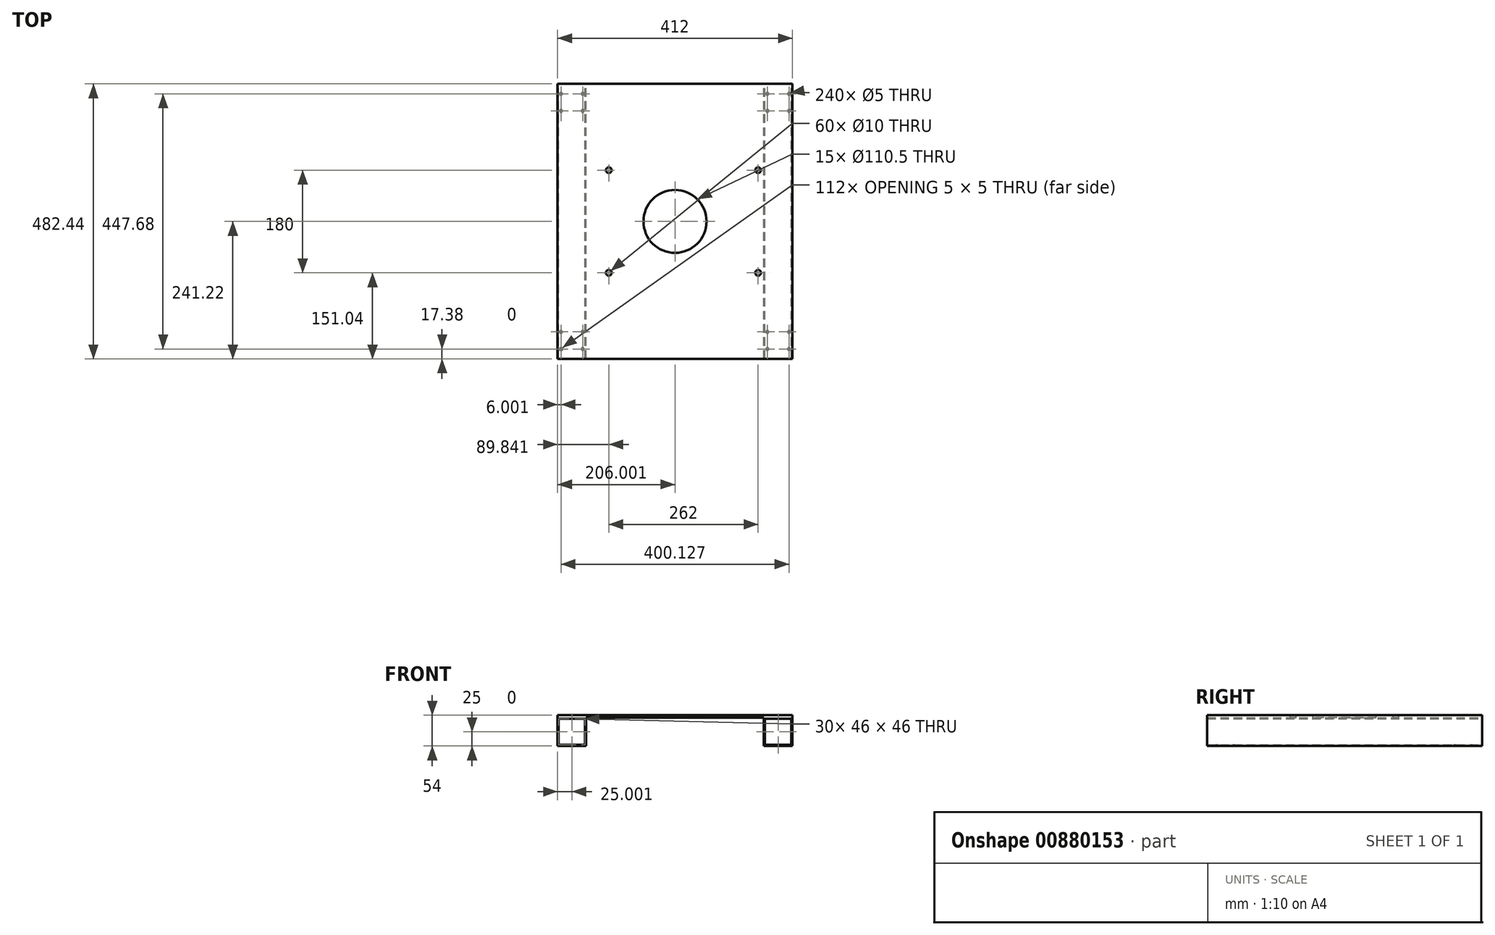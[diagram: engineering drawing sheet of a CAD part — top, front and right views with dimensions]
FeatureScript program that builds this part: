
annotation { "Feature Type Name" : "Feature", "Feature Type Description" : "" }
export const myFeature = defineFeature(function(context is Context, id is Id, definition is map)
    precondition{}
    {
        {
            var Q0;
            Q0=qCreatedBy(makeId("Front.planeOp"),FACE);
            var sketch = newSketch(context, id + "F0", { "sketchPlane" : qUnion([Q0])});
            skLineSegment(sketch, "E0", {"start": v(352.9, 0) * mm, "end": v(-59.1, 0) * mm});
            skLineSegment(sketch, "E1", {"start": v(-59.1, 0) * mm, "end": v(-59.1, -4) * mm});
            skLineSegment(sketch, "E2", {"start": v(-59.1, -4) * mm, "end": v(352.9, -4) * mm});
            skLineSegment(sketch, "E3", {"start": v(352.9, -4) * mm, "end": v(352.9, 0) * mm});
            skLineSegment(sketch, "E4", {"start": v(-59.1, -4) * mm, "end": v(-59.1, -54) * mm});
            skLineSegment(sketch, "E5", {"start": v(-59.1, -54) * mm, "end": v(-9.1, -54) * mm});
            skLineSegment(sketch, "E6", {"start": v(-9.1, -54) * mm, "end": v(-9.1, -4) * mm});
            skLineSegment(sketch, "E7", {"start": v(352.9, -4) * mm, "end": v(352.9, -54) * mm});
            skLineSegment(sketch, "E8", {"start": v(352.9, -54) * mm, "end": v(302.9, -54) * mm});
            skLineSegment(sketch, "E9", {"start": v(302.9, -54) * mm, "end": v(302.9, -4) * mm});
            skLineSegment(sketch, "E10", {"start": v(-59.1, -4) * mm, "end": v(-57.1, -4) * mm});
            skLineSegment(sketch, "E11", {"start": v(-57.1, -4) * mm, "end": v(-57.1, -52) * mm});
            skLineSegment(sketch, "E12", {"start": v(-57.1, -52) * mm, "end": v(-11.1, -52) * mm});
            skLineSegment(sketch, "E13", {"start": v(-11.1, -52) * mm, "end": v(-11.1, -6) * mm});
            skLineSegment(sketch, "E14", {"start": v(-11.1, -6) * mm, "end": v(-57.1, -6) * mm});
            skLineSegment(sketch, "E15", {"start": v(302.9, -4) * mm, "end": v(304.9, -4) * mm});
            skLineSegment(sketch, "E16", {"start": v(304.9, -4) * mm, "end": v(304.9, -52) * mm});
            skLineSegment(sketch, "E17", {"start": v(304.9, -52) * mm, "end": v(350.9, -52) * mm});
            skLineSegment(sketch, "E18", {"start": v(350.9, -52) * mm, "end": v(350.9, -6) * mm});
            skLineSegment(sketch, "E19", {"start": v(350.9, -6) * mm, "end": v(304.9, -6) * mm});
            skSolve(sketch);
        }
        {
            var Q0;
            {var subQ1=sQuery(id+"F0.wireOp",EDGE,"E7");Q0=makeQuery(id+"F0.imprint","IMPRINT",FACE,{"disambiguationData":[TD([[makeQuery(id+"F0.imprint","IMPRINT",EDGE,{"derivedFrom":subQ1}),-1.0]])]});}
            var Q1;
            Q1=makeQuery(id+"F0.imprint","IMPRINT",FACE,{"disambiguationData":[TD([[makeQuery(id+"F0.imprint","IMPRINT",EDGE,{"derivedFrom":sQuery(id+"F0.wireOp",EDGE,"E0")}),1.0]])]});
            var Q2;
            Q2=makeQuery(id+"F0.imprint","IMPRINT",FACE,{"disambiguationData":[TD([[makeQuery(id+"F0.imprint","IMPRINT",EDGE,{"derivedFrom":sQuery(id+"F0.wireOp",EDGE,"E4")}),1.0]])]});
            extrude(context, id + "F1", {"entities" : qUnion([Q0, Q1, Q2]), "depth" : 482.44 * mm, "offsetDistance" : 25 * mm});
        }
        {
            var Q0;
            Q0=makeQuery(id+"F1.opExtrude","SWEPT_FACE",FACE,{"disambiguationData":[OSD([sQuery(id+"F0.wireOp",EDGE,"E0")])]});
            var sketch = newSketch(context, id + "F2", { "sketchPlane" : qUnion([Q0])});
            skLineSegment(sketch, "E20", {"start": v(146.9, 0) * mm, "end": v(146.9, -482.44) * mm});
            skLineSegment(sketch, "E21", {"start": v(-59.1, -241.22) * mm, "end": v(352.9, -241.22) * mm});
            skCircle(sketch, "E22", {"center": v(146.9, -241.22) * mm, "radius": 55.25 * mm});
            skSolve(sketch);
        }
        {
            var Q0;
            Q0 = qSketchRegion(id + "F2", true);
            extrude(context, id + "F3", {"entities" : qUnion([Q0]), "operationType" : NewBodyOperationType.REMOVE, "oppositeDirection" : true, "depth" : 25 * mm, "offsetDistance" : 25 * mm});
        }
        {
            var Q0;
            Q0=makeQuery(id+"F1.opExtrude","SWEPT_FACE",FACE,{"disambiguationData":[OSD([sQuery(id+"F0.wireOp",EDGE,"E5")])]});
            var sketch = newSketch(context, id + "F4", { "sketchPlane" : qUnion([Q0])});
            skLineSegment(sketch, "E23", {"start": v(-59.1, 0) * mm, "end": v(-59.1, 17.38) * mm});
            skLineSegment(sketch, "E24", {"start": v(-59.1, 17.38) * mm, "end": v(-52.97, 17.38) * mm});
            skLineSegment(sketch, "E25", {"start": v(-52.97, 17.38) * mm, "end": v(-52.97, 47.38) * mm});
            skLineSegment(sketch, "E26", {"start": v(-52.97, 47.38) * mm, "end": v(-14.97, 47.38) * mm});
            skLineSegment(sketch, "E27", {"start": v(-14.97, 47.38) * mm, "end": v(-14.97, 17.38) * mm});
            skCircle(sketch, "E28", {"center": v(-52.97, 47.38) * mm, "radius": 2.5 * mm});
            skCircle(sketch, "E29", {"center": v(-52.97, 17.38) * mm, "radius": 2.5 * mm});
            skCircle(sketch, "E30", {"center": v(-14.97, 47.38) * mm, "radius": 2.5 * mm});
            skCircle(sketch, "E31", {"center": v(-14.97, 17.38) * mm, "radius": 2.5 * mm});
            skLineSegment(sketch, "E32", {"start": v(302.9, 0) * mm, "end": v(302.9, 17.38) * mm});
            skLineSegment(sketch, "E33", {"start": v(302.9, 17.38) * mm, "end": v(309.03, 17.38) * mm});
            skLineSegment(sketch, "E34", {"start": v(309.03, 17.38) * mm, "end": v(309.03, 47.38) * mm});
            skLineSegment(sketch, "E35", {"start": v(309.03, 47.38) * mm, "end": v(347.03, 47.38) * mm});
            skLineSegment(sketch, "E36", {"start": v(347.03, 47.38) * mm, "end": v(347.03, 17.38) * mm});
            skCircle(sketch, "E37", {"center": v(309.03, 47.38) * mm, "radius": 2.5 * mm});
            skCircle(sketch, "E38", {"center": v(309.03, 17.38) * mm, "radius": 2.5 * mm});
            skCircle(sketch, "E39", {"center": v(347.03, 47.38) * mm, "radius": 2.5 * mm});
            skCircle(sketch, "E40", {"center": v(347.03, 17.38) * mm, "radius": 2.5 * mm});
            skSolve(sketch);
        }
        {
            var Q0;
            {var subQ0=sQuery(id+"F4.wireOp",EDGE,"E27");var subQ1=sQuery(id+"F4.wireOp",EDGE,"E26");var subQ2=makeQuery(id+"F4.imprint","INTERSECT",VERTEX,{"derivedFrom":[subQ1,subQ0]});Q0=makeQuery(id+"F4.imprint","IMPRINT",FACE,{"disambiguationData":[TD([[makeQuery(id+"F4.imprint","IMPRINT",EDGE,{"disambiguationData":[TD([[subQ2,1.0]])],"derivedFrom":subQ1}),-1.0]])]});}
            var Q1;
            {var subQ0=sQuery(id+"F4.wireOp",EDGE,"E27");var subQ1=sQuery(id+"F4.wireOp",EDGE,"E26");var subQ2=makeQuery(id+"F4.imprint","INTERSECT",VERTEX,{"derivedFrom":[subQ1,subQ0]});Q1=makeQuery(id+"F4.imprint","IMPRINT",FACE,{"disambiguationData":[TD([[makeQuery(id+"F4.imprint","IMPRINT",EDGE,{"disambiguationData":[TD([[subQ2,1.0]])],"derivedFrom":subQ1}),1.0]])]});}
            var Q2;
            {var subQ0=sQuery(id+"F4.wireOp",EDGE,"E26");var subQ1=sQuery(id+"F4.wireOp",EDGE,"E25");var subQ2=makeQuery(id+"F4.imprint","INTERSECT",VERTEX,{"derivedFrom":[subQ1,subQ0]});Q2=makeQuery(id+"F4.imprint","IMPRINT",FACE,{"disambiguationData":[TD([[makeQuery(id+"F4.imprint","IMPRINT",EDGE,{"disambiguationData":[TD([[subQ2,1.0]])],"derivedFrom":subQ1}),1.0]])]});}
            var Q3;
            {var subQ0=sQuery(id+"F4.wireOp",EDGE,"E26");var subQ1=sQuery(id+"F4.wireOp",EDGE,"E25");var subQ2=makeQuery(id+"F4.imprint","INTERSECT",VERTEX,{"derivedFrom":[subQ1,subQ0]});Q3=makeQuery(id+"F4.imprint","IMPRINT",FACE,{"disambiguationData":[TD([[makeQuery(id+"F4.imprint","IMPRINT",EDGE,{"disambiguationData":[TD([[subQ2,1.0]])],"derivedFrom":subQ1}),-1.0]])]});}
            var Q4;
            {var subQ0=sQuery(id+"F4.wireOp",EDGE,"E25");var subQ1=sQuery(id+"F4.wireOp",EDGE,"E24");var subQ2=makeQuery(id+"F4.imprint","INTERSECT",VERTEX,{"derivedFrom":[subQ1,subQ0]});Q4=makeQuery(id+"F4.imprint","IMPRINT",FACE,{"disambiguationData":[TD([[makeQuery(id+"F4.imprint","IMPRINT",EDGE,{"disambiguationData":[TD([[subQ2,1.0]])],"derivedFrom":subQ1}),1.0]])]});}
            var Q5;
            {var subQ0=sQuery(id+"F4.wireOp",EDGE,"E25");var subQ1=sQuery(id+"F4.wireOp",EDGE,"E24");var subQ2=makeQuery(id+"F4.imprint","INTERSECT",VERTEX,{"derivedFrom":[subQ1,subQ0]});Q5=makeQuery(id+"F4.imprint","IMPRINT",FACE,{"disambiguationData":[TD([[makeQuery(id+"F4.imprint","IMPRINT",EDGE,{"disambiguationData":[TD([[subQ2,1.0]])],"derivedFrom":subQ1}),-1.0]])]});}
            var Q6;
            Q6=makeQuery(id+"F4.imprint","IMPRINT",FACE,{"disambiguationData":[TD([[makeQuery(id+"F4.imprint","IMPRINT",EDGE,{"derivedFrom":sQuery(id+"F4.wireOp",EDGE,"E31")}),1.0]])]});
            var Q7;
            Q7=sQuery(id+"F4.wireOp",EDGE,"E28");
            var Q8;
            Q8=sQuery(id+"F4.wireOp",EDGE,"E30");
            var Q9;
            Q9=sQuery(id+"F4.wireOp",EDGE,"E29");
            var Q10;
            Q10=sQuery(id+"F4.wireOp",EDGE,"E31");
            extrude(context, id + "F5", {"entities" : qUnion([Q0, Q1, Q2, Q3, Q4, Q5, Q6]), "operationType" : NewBodyOperationType.REMOVE, "surfaceEntities" : qUnion([Q7, Q8, Q9, Q10]), "oppositeDirection" : true, "depth" : 25 * mm, "offsetDistance" : 25 * mm});
        }
        {
            var Q0;
            Q0=makeQuery(id+"F1.opExtrude","SWEPT_FACE",FACE,{"disambiguationData":[OSD([sQuery(id+"F0.wireOp",EDGE,"E5")])]});
            var sketch = newSketch(context, id + "F6", { "sketchPlane" : qUnion([Q0])});
            skLineSegment(sketch, "E41", {"start": v(302.87, 482.44) * mm, "end": v(302.87, 465.06) * mm});
            skLineSegment(sketch, "E42", {"start": v(302.87, 465.06) * mm, "end": v(309, 465.06) * mm});
            skLineSegment(sketch, "E43", {"start": v(309, 465.06) * mm, "end": v(309, 435.06) * mm});
            skLineSegment(sketch, "E44", {"start": v(309, 435.06) * mm, "end": v(347, 435.06) * mm});
            skLineSegment(sketch, "E45", {"start": v(347, 435.06) * mm, "end": v(347, 465.06) * mm});
            skCircle(sketch, "E46", {"center": v(309, 465.06) * mm, "radius": 2.5 * mm});
            skCircle(sketch, "E47", {"center": v(309, 435.06) * mm, "radius": 2.5 * mm});
            skCircle(sketch, "E48", {"center": v(347, 465.06) * mm, "radius": 2.5 * mm});
            skCircle(sketch, "E49", {"center": v(347, 435.06) * mm, "radius": 2.5 * mm});
            skLineSegment(sketch, "E50", {"start": v(-59.23, 482.44) * mm, "end": v(-59.23, 465.06) * mm});
            skLineSegment(sketch, "E51", {"start": v(-59.23, 465.06) * mm, "end": v(-53.1, 465.06) * mm});
            skLineSegment(sketch, "E52", {"start": v(-53.1, 465.06) * mm, "end": v(-53.1, 435.06) * mm});
            skLineSegment(sketch, "E53", {"start": v(-53.1, 435.06) * mm, "end": v(-15.1, 435.06) * mm});
            skLineSegment(sketch, "E54", {"start": v(-15.1, 435.06) * mm, "end": v(-15.1, 465.06) * mm});
            skCircle(sketch, "E55", {"center": v(-53.1, 465.06) * mm, "radius": 2.5 * mm});
            skCircle(sketch, "E56", {"center": v(-53.1, 435.06) * mm, "radius": 2.5 * mm});
            skCircle(sketch, "E57", {"center": v(-15.1, 465.06) * mm, "radius": 2.5 * mm});
            skCircle(sketch, "E58", {"center": v(-15.1, 435.06) * mm, "radius": 2.5 * mm});
            skSolve(sketch);
        }
        {
            var Q0;
            Q0=makeQuery(id+"F6.imprint","IMPRINT",FACE,{"disambiguationData":[TD([[makeQuery(id+"F6.imprint","IMPRINT",EDGE,{"derivedFrom":sQuery(id+"F6.wireOp",EDGE,"E48")}),1.0]])]});
            var Q1;
            {var subQ0=sQuery(id+"F6.wireOp",EDGE,"E45");var subQ1=sQuery(id+"F6.wireOp",EDGE,"E44");var subQ2=makeQuery(id+"F6.imprint","INTERSECT",VERTEX,{"derivedFrom":[subQ1,subQ0]});Q1=makeQuery(id+"F6.imprint","IMPRINT",FACE,{"disambiguationData":[TD([[makeQuery(id+"F6.imprint","IMPRINT",EDGE,{"disambiguationData":[TD([[subQ2,1.0]])],"derivedFrom":subQ1}),-1.0]])]});}
            var Q2;
            {var subQ0=sQuery(id+"F6.wireOp",EDGE,"E45");var subQ1=sQuery(id+"F6.wireOp",EDGE,"E44");var subQ2=makeQuery(id+"F6.imprint","INTERSECT",VERTEX,{"derivedFrom":[subQ1,subQ0]});Q2=makeQuery(id+"F6.imprint","IMPRINT",FACE,{"disambiguationData":[TD([[makeQuery(id+"F6.imprint","IMPRINT",EDGE,{"disambiguationData":[TD([[subQ2,1.0]])],"derivedFrom":subQ1}),1.0]])]});}
            var Q3;
            {var subQ0=sQuery(id+"F6.wireOp",EDGE,"E44");var subQ1=sQuery(id+"F6.wireOp",EDGE,"E43");var subQ2=makeQuery(id+"F6.imprint","INTERSECT",VERTEX,{"derivedFrom":[subQ1,subQ0]});Q3=makeQuery(id+"F6.imprint","IMPRINT",FACE,{"disambiguationData":[TD([[makeQuery(id+"F6.imprint","IMPRINT",EDGE,{"disambiguationData":[TD([[subQ2,1.0]])],"derivedFrom":subQ1}),-1.0]])]});}
            var Q4;
            {var subQ0=sQuery(id+"F6.wireOp",EDGE,"E44");var subQ1=sQuery(id+"F6.wireOp",EDGE,"E43");var subQ2=makeQuery(id+"F6.imprint","INTERSECT",VERTEX,{"derivedFrom":[subQ1,subQ0]});Q4=makeQuery(id+"F6.imprint","IMPRINT",FACE,{"disambiguationData":[TD([[makeQuery(id+"F6.imprint","IMPRINT",EDGE,{"disambiguationData":[TD([[subQ2,1.0]])],"derivedFrom":subQ1}),1.0]])]});}
            var Q5;
            {var subQ0=sQuery(id+"F6.wireOp",EDGE,"E43");var subQ1=sQuery(id+"F6.wireOp",EDGE,"E42");var subQ2=makeQuery(id+"F6.imprint","INTERSECT",VERTEX,{"derivedFrom":[subQ1,subQ0]});Q5=makeQuery(id+"F6.imprint","IMPRINT",FACE,{"disambiguationData":[TD([[makeQuery(id+"F6.imprint","IMPRINT",EDGE,{"disambiguationData":[TD([[subQ2,1.0]])],"derivedFrom":subQ1}),-1.0]])]});}
            var Q6;
            {var subQ0=sQuery(id+"F6.wireOp",EDGE,"E43");var subQ1=sQuery(id+"F6.wireOp",EDGE,"E42");var subQ2=makeQuery(id+"F6.imprint","INTERSECT",VERTEX,{"derivedFrom":[subQ1,subQ0]});Q6=makeQuery(id+"F6.imprint","IMPRINT",FACE,{"disambiguationData":[TD([[makeQuery(id+"F6.imprint","IMPRINT",EDGE,{"disambiguationData":[TD([[subQ2,1.0]])],"derivedFrom":subQ1}),1.0]])]});}
            var Q7;
            Q7=sQuery(id+"F6.wireOp",EDGE,"E46");
            var Q8;
            Q8=sQuery(id+"F6.wireOp",EDGE,"E47");
            var Q9;
            Q9=sQuery(id+"F6.wireOp",EDGE,"E49");
            var Q10;
            Q10=sQuery(id+"F6.wireOp",EDGE,"E48");
            extrude(context, id + "F7", {"entities" : qUnion([Q0, Q1, Q2, Q3, Q4, Q5, Q6]), "operationType" : NewBodyOperationType.REMOVE, "surfaceEntities" : qUnion([Q7, Q8, Q9, Q10]), "oppositeDirection" : true, "depth" : 25 * mm, "offsetDistance" : 25 * mm});
        }
        {
            var Q0;
            Q0=makeQuery(id+"F6.imprint","IMPRINT",FACE,{"disambiguationData":[TD([[makeQuery(id+"F6.imprint","IMPRINT",EDGE,{"derivedFrom":sQuery(id+"F6.wireOp",EDGE,"E57")}),1.0]])]});
            var Q1;
            {var subQ0=sQuery(id+"F6.wireOp",EDGE,"E52");var subQ1=sQuery(id+"F6.wireOp",EDGE,"E51");var subQ2=makeQuery(id+"F6.imprint","INTERSECT",VERTEX,{"derivedFrom":[subQ1,subQ0]});Q1=makeQuery(id+"F6.imprint","IMPRINT",FACE,{"disambiguationData":[TD([[makeQuery(id+"F6.imprint","IMPRINT",EDGE,{"disambiguationData":[TD([[subQ2,1.0]])],"derivedFrom":subQ1}),1.0]])]});}
            var Q2;
            {var subQ0=sQuery(id+"F6.wireOp",EDGE,"E52");var subQ1=sQuery(id+"F6.wireOp",EDGE,"E51");var subQ2=makeQuery(id+"F6.imprint","INTERSECT",VERTEX,{"derivedFrom":[subQ1,subQ0]});Q2=makeQuery(id+"F6.imprint","IMPRINT",FACE,{"disambiguationData":[TD([[makeQuery(id+"F6.imprint","IMPRINT",EDGE,{"disambiguationData":[TD([[subQ2,1.0]])],"derivedFrom":subQ1}),-1.0]])]});}
            var Q3;
            {var subQ0=sQuery(id+"F6.wireOp",EDGE,"E53");var subQ1=sQuery(id+"F6.wireOp",EDGE,"E52");var subQ2=makeQuery(id+"F6.imprint","INTERSECT",VERTEX,{"derivedFrom":[subQ1,subQ0]});Q3=makeQuery(id+"F6.imprint","IMPRINT",FACE,{"disambiguationData":[TD([[makeQuery(id+"F6.imprint","IMPRINT",EDGE,{"disambiguationData":[TD([[subQ2,1.0]])],"derivedFrom":subQ1}),-1.0]])]});}
            var Q4;
            {var subQ0=sQuery(id+"F6.wireOp",EDGE,"E53");var subQ1=sQuery(id+"F6.wireOp",EDGE,"E52");var subQ2=makeQuery(id+"F6.imprint","INTERSECT",VERTEX,{"derivedFrom":[subQ1,subQ0]});Q4=makeQuery(id+"F6.imprint","IMPRINT",FACE,{"disambiguationData":[TD([[makeQuery(id+"F6.imprint","IMPRINT",EDGE,{"disambiguationData":[TD([[subQ2,1.0]])],"derivedFrom":subQ1}),1.0]])]});}
            var Q5;
            {var subQ0=sQuery(id+"F6.wireOp",EDGE,"E54");var subQ1=sQuery(id+"F6.wireOp",EDGE,"E53");var subQ2=makeQuery(id+"F6.imprint","INTERSECT",VERTEX,{"derivedFrom":[subQ1,subQ0]});Q5=makeQuery(id+"F6.imprint","IMPRINT",FACE,{"disambiguationData":[TD([[makeQuery(id+"F6.imprint","IMPRINT",EDGE,{"disambiguationData":[TD([[subQ2,1.0]])],"derivedFrom":subQ1}),1.0]])]});}
            var Q6;
            {var subQ0=sQuery(id+"F6.wireOp",EDGE,"E54");var subQ1=sQuery(id+"F6.wireOp",EDGE,"E53");var subQ2=makeQuery(id+"F6.imprint","INTERSECT",VERTEX,{"derivedFrom":[subQ1,subQ0]});Q6=makeQuery(id+"F6.imprint","IMPRINT",FACE,{"disambiguationData":[TD([[makeQuery(id+"F6.imprint","IMPRINT",EDGE,{"disambiguationData":[TD([[subQ2,1.0]])],"derivedFrom":subQ1}),-1.0]])]});}
            var Q7;
            Q7=sQuery(id+"F6.wireOp",EDGE,"E57");
            var Q8;
            Q8=sQuery(id+"F6.wireOp",EDGE,"E55");
            var Q9;
            Q9=sQuery(id+"F6.wireOp",EDGE,"E58");
            var Q10;
            Q10=sQuery(id+"F6.wireOp",EDGE,"E56");
            extrude(context, id + "F8", {"entities" : qUnion([Q0, Q1, Q2, Q3, Q4, Q5, Q6]), "operationType" : NewBodyOperationType.REMOVE, "surfaceEntities" : qUnion([Q7, Q8, Q9, Q10]), "oppositeDirection" : true, "depth" : 25 * mm, "offsetDistance" : 25 * mm});
        }
        {
            var Q0;
            Q0 = qSketchRegion(id + "F4", true);
            extrude(context, id + "F9", {"entities" : qUnion([Q0]), "operationType" : NewBodyOperationType.REMOVE, "oppositeDirection" : true, "depth" : 25 * mm, "offsetDistance" : 25 * mm});
        }
        {
            var Q0;
            Q0=makeQuery(id+"F1.opExtrude","SWEPT_FACE",FACE,{"disambiguationData":[OSD([sQuery(id+"F0.wireOp",EDGE,"E0")])]});
            var sketch = newSketch(context, id + "F10", { "sketchPlane" : qUnion([Q0])});
            skLineSegment(sketch, "E59", {"start": v(-29.4, -482.44) * mm, "end": v(30.74, -482.44) * mm});
            skLineSegment(sketch, "E60", {"start": v(30.74, -482.44) * mm, "end": v(30.74, -331.4) * mm});
            skLineSegment(sketch, "E61", {"start": v(30.74, -331.4) * mm, "end": v(30.74, -151.4) * mm});
            skLineSegment(sketch, "E62", {"start": v(30.74, -151.4) * mm, "end": v(292.74, -151.4) * mm});
            skLineSegment(sketch, "E63", {"start": v(292.74, -151.4) * mm, "end": v(292.74, -331.4) * mm});
            skCircle(sketch, "E64", {"center": v(30.74, -151.4) * mm, "radius": 5 * mm});
            skCircle(sketch, "E65", {"center": v(30.74, -331.4) * mm, "radius": 5 * mm});
            skCircle(sketch, "E66", {"center": v(292.74, -331.4) * mm, "radius": 5 * mm});
            skCircle(sketch, "E67", {"center": v(292.74, -151.4) * mm, "radius": 5 * mm});
            skLineSegment(sketch, "E68", {"start": v(352.9, -482.44) * mm, "end": v(292.76, -482.44) * mm});
            skLineSegment(sketch, "E69", {"start": v(292.76, -482.44) * mm, "end": v(292.76, -331.4) * mm});
            skSolve(sketch);
        }
        {
            var Q0;
            Q0 = qSketchRegion(id + "F10", true);
            extrude(context, id + "F11", {"entities" : qUnion([Q0]), "operationType" : NewBodyOperationType.REMOVE, "oppositeDirection" : true, "depth" : 25 * mm, "offsetDistance" : 25 * mm});
        }
        {
            var Q0;
            Q0 = qSketchRegion(id + "F10", true);
            extrude(context, id + "F12", {"entities" : qUnion([Q0]), "operationType" : NewBodyOperationType.REMOVE, "oppositeDirection" : true, "depth" : 25 * mm, "offsetDistance" : 25 * mm});
        }
    });
